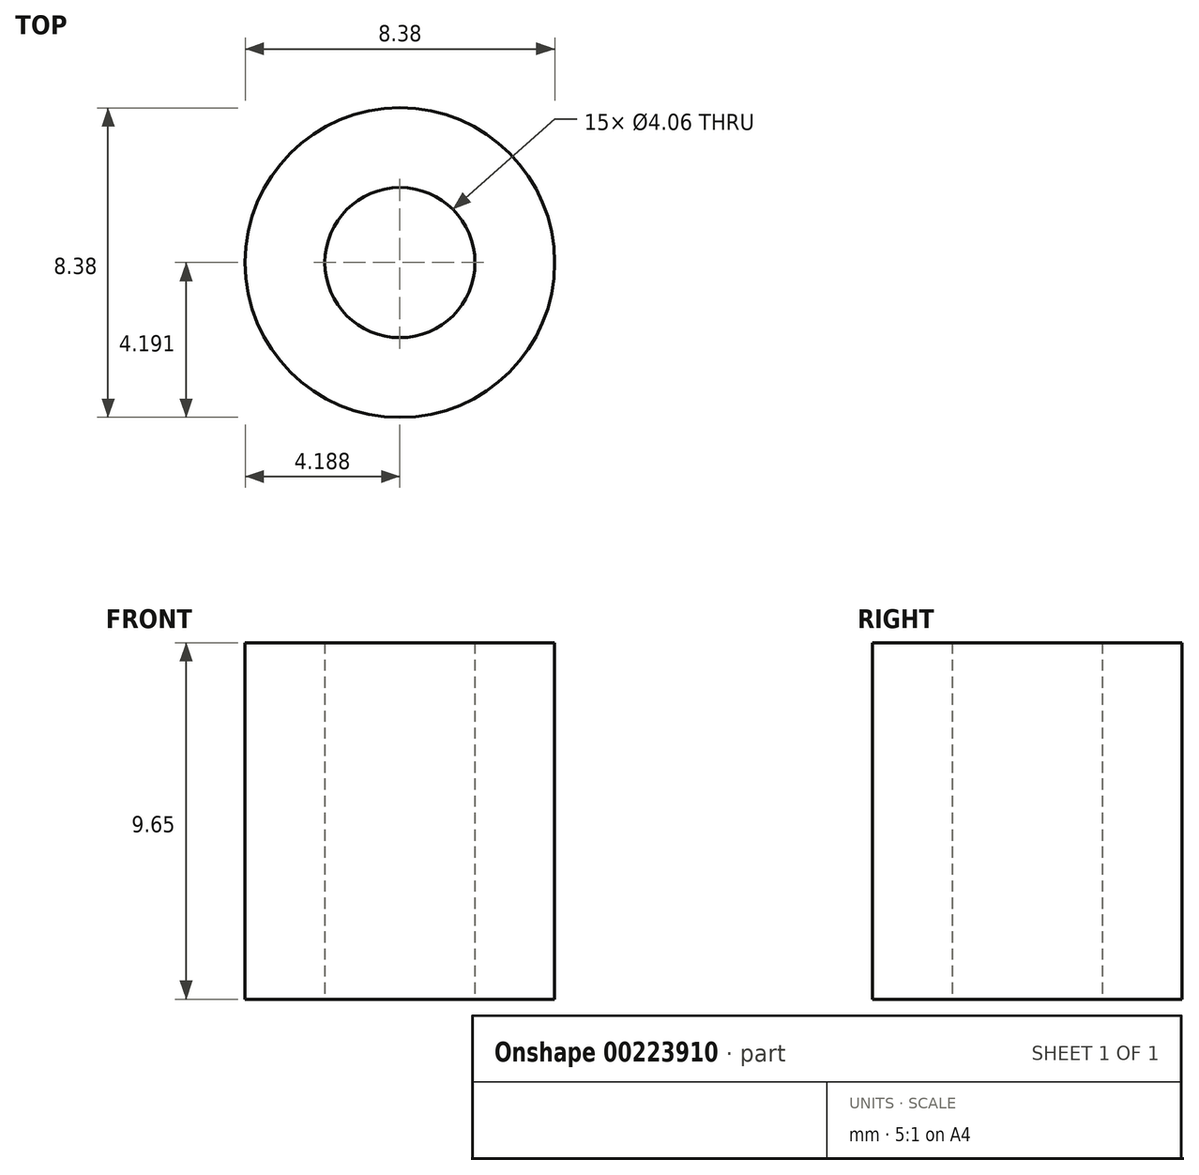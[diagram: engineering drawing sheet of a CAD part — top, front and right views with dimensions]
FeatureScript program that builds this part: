
annotation { "Feature Type Name" : "Feature", "Feature Type Description" : "" }
export const myFeature = defineFeature(function(context is Context, id is Id, definition is map)
    precondition{}
    {
        {
            var Q0;
            Q0=qCreatedBy(makeId("Top.planeOp"),FACE);
            var sketch = newSketch(context, id + "F0", { "sketchPlane" : qUnion([Q0])});
            skCircle(sketch, "E0", {"center": v(-24.5, 13.55) * mm, "radius": 2.03 * mm});
            skCircle(sketch, "E1", {"center": v(-24.5, 13.55) * mm, "radius": 4.2 * mm});
            skSolve(sketch);
        }
        {
            var Q0;
            Q0 = qSketchRegion(id + "F0", true);
            extrude(context, id + "F1", {"entities" : qUnion([Q0]), "depth" : 9.65 * mm});
        }
    });
